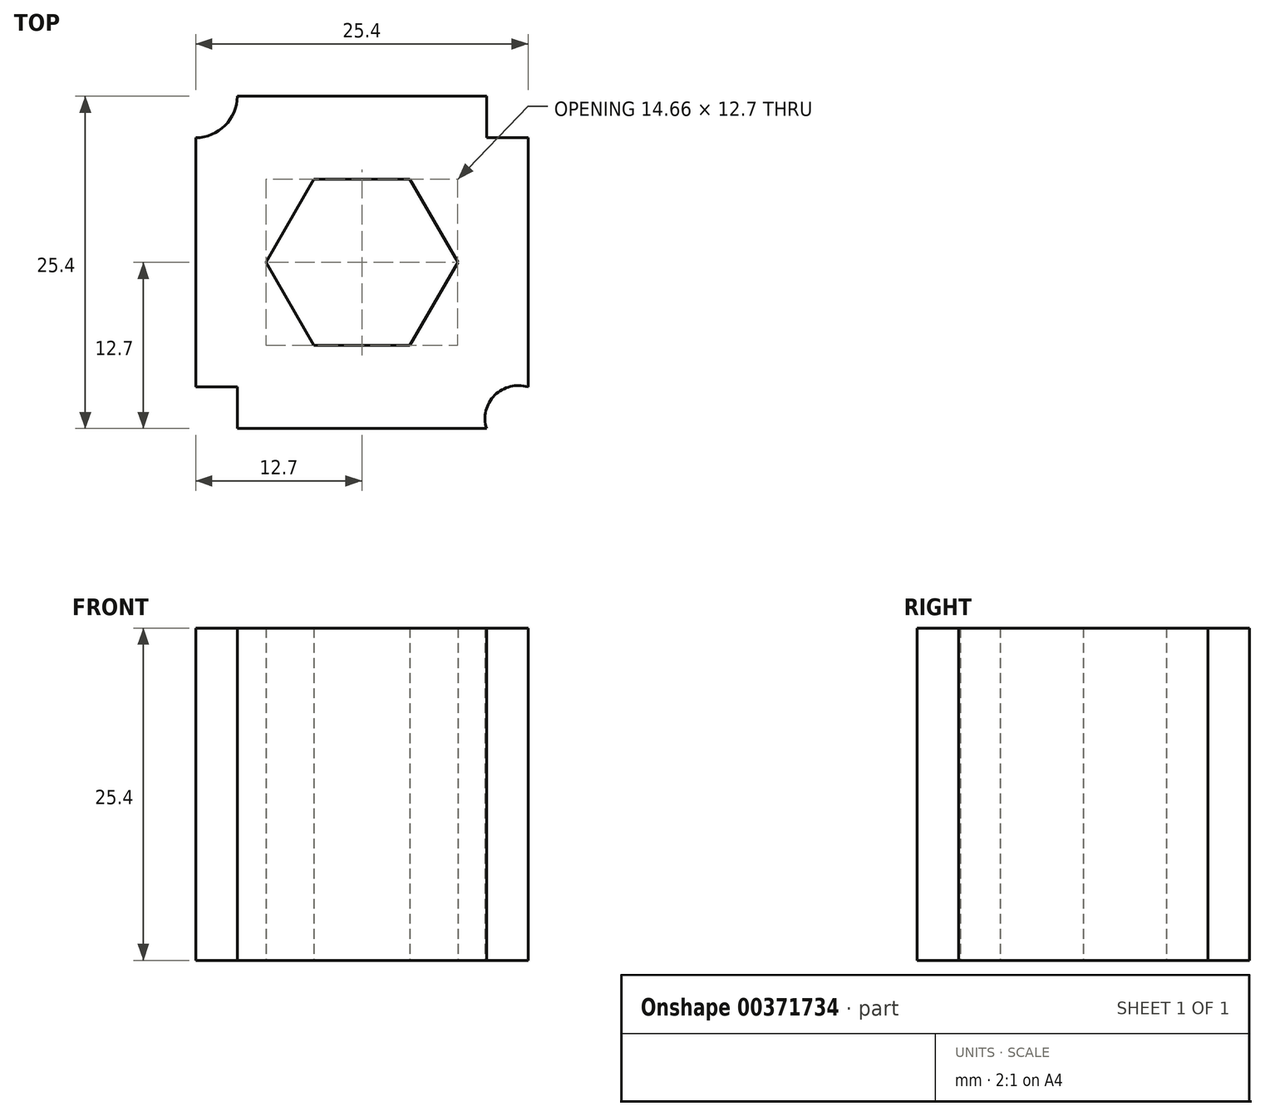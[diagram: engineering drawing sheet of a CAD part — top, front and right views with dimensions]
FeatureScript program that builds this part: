
annotation { "Feature Type Name" : "Feature", "Feature Type Description" : "" }
export const myFeature = defineFeature(function(context is Context, id is Id, definition is map)
    precondition{}
    {
        {
            var Q0;
            Q0=qCreatedBy(makeId("Top.planeOp"),FACE);
            var sketch = newSketch(context, id + "F0", { "sketchPlane" : qUnion([Q0])});
            skLineSegment(sketch, "E0.bottom", {"start": v(12.7, 12.7) * mm, "end": v(-12.7, 12.7) * mm});
            skLineSegment(sketch, "E0.top", {"start": v(12.7, -12.7) * mm, "end": v(-12.7, -12.7) * mm});
            skLineSegment(sketch, "E0.left", {"start": v(12.7, 12.7) * mm, "end": v(12.7, -12.7) * mm});
            skLineSegment(sketch, "E0.right", {"start": v(-12.7, 12.7) * mm, "end": v(-12.7, -12.7) * mm});
            skPoint(sketch, "E0.middle", {"position": v(0, 0) * mm});
            skLineSegment(sketch, "E1.bottom", {"start": v(12.7, 12.7) * mm, "end": v(9.52, 12.7) * mm});
            skLineSegment(sketch, "E1.top", {"start": v(12.7, 9.53) * mm, "end": v(9.52, 9.53) * mm});
            skLineSegment(sketch, "E1.left", {"start": v(12.7, 12.7) * mm, "end": v(12.7, 9.53) * mm});
            skLineSegment(sketch, "E1.right", {"start": v(9.52, 12.7) * mm, "end": v(9.52, 9.53) * mm});
            skLineSegment(sketch, "E2.bottom", {"start": v(-12.7, -12.7) * mm, "end": v(-9.52, -12.7) * mm});
            skLineSegment(sketch, "E2.top", {"start": v(-12.7, -9.53) * mm, "end": v(-9.52, -9.53) * mm});
            skLineSegment(sketch, "E2.left", {"start": v(-12.7, -12.7) * mm, "end": v(-12.7, -9.53) * mm});
            skLineSegment(sketch, "E2.right", {"start": v(-9.52, -12.7) * mm, "end": v(-9.52, -9.53) * mm});
            skArc(sketch, "E3", {"start": v(12.7, -9.52) * mm, "mid": v(10.16, -10.16) * mm, "end": v(9.53, -12.7) * mm});
            skArc(sketch, "E4", {"start": v(-12.7, 9.52) * mm, "mid": v(-10.45, 10.45) * mm, "end": v(-9.53, 12.7) * mm});
            skCircle(sketch, "E5.cCircle", {"center": v(0, 0) * mm, "radius": 6.35 * mm, "construction": true});
            skLineSegment(sketch, "E5.0", {"start": v(3.67, 6.35) * mm, "end": v(7.33, 0) * mm});
            skLineSegment(sketch, "E5.1", {"start": v(7.33, 0) * mm, "end": v(3.67, -6.35) * mm});
            skLineSegment(sketch, "E5.2", {"start": v(3.67, -6.35) * mm, "end": v(-3.67, -6.35) * mm});
            skLineSegment(sketch, "E5.3", {"start": v(-3.67, -6.35) * mm, "end": v(-7.33, 0) * mm});
            skLineSegment(sketch, "E5.4", {"start": v(-7.33, 0) * mm, "end": v(-3.67, 6.35) * mm});
            skLineSegment(sketch, "E5.5", {"start": v(-3.67, 6.35) * mm, "end": v(3.67, 6.35) * mm});
            skPoint(sketch, "E5.0.midPoint", {"position": v(5.5, 3.17) * mm});
            skSolve(sketch);
        }
        {
            var Q0;
            {var subQ3=sQuery(id+"F0.wireOp",EDGE,"E1.top");Q0=makeQuery(id+"F0.imprint","IMPRINT",FACE,{"disambiguationData":[TD([[makeQuery(id+"F0.imprint","IMPRINT",EDGE,{"derivedFrom":subQ3}),1.0]])]});}
            extrude(context, id + "F1", {"entities" : qUnion([Q0]), "depth" : 25.4 * mm});
        }
    });
